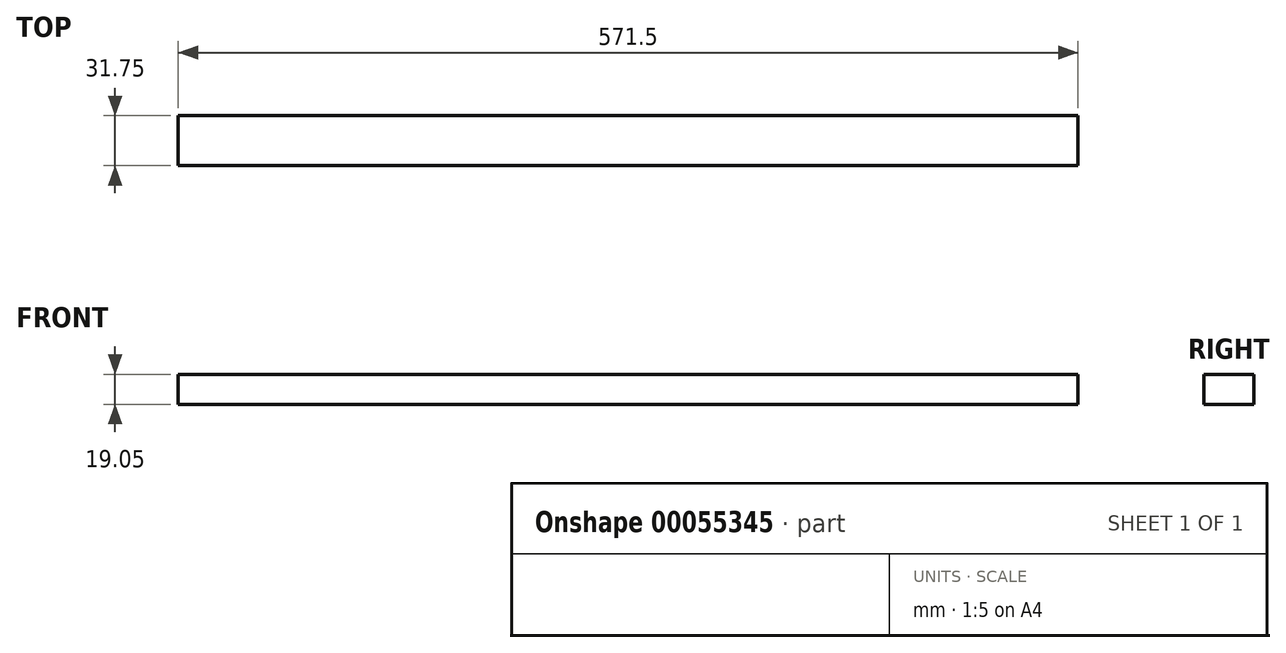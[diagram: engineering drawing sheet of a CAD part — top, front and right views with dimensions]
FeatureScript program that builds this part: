
annotation { "Feature Type Name" : "Feature", "Feature Type Description" : "" }
export const myFeature = defineFeature(function(context is Context, id is Id, definition is map)
    precondition{}
    {
        {
            var Q0;
            Q0=qCreatedBy(makeId("Front.planeOp"),FACE);
            var sketch = newSketch(context, id + "F0", { "sketchPlane" : qUnion([Q0])});
            skLineSegment(sketch, "E0.bottom", {"start": v(0, 0) * mm, "end": v(571.5, 0) * mm});
            skLineSegment(sketch, "E0.top", {"start": v(0, 19.05) * mm, "end": v(571.5, 19.05) * mm});
            skLineSegment(sketch, "E0.left", {"start": v(0, 0) * mm, "end": v(0, 19.05) * mm});
            skLineSegment(sketch, "E0.right", {"start": v(571.5, 0) * mm, "end": v(571.5, 19.05) * mm});
            skSolve(sketch);
        }
        {
            var Q0;
            Q0=makeQuery(id+"F0.imprint","IMPRINT",FACE,{"disambiguationData":[TD([[makeQuery(id+"F0.imprint","IMPRINT",EDGE,{"derivedFrom":sQuery(id+"F0.wireOp",EDGE,"E0.bottom")}),1.0]])]});
            extrude(context, id + "F1", {"entities" : qUnion([Q0]), "oppositeDirection" : true, "depth" : 31.75 * mm});
        }
        {
            var Q0;
            Q0=makeQuery(id+"F1.opExtrude","SWEPT_BODY",BODY,{"disambiguationData":[OSD([sQuery(id+"F0.wireOp",EDGE,"E0.bottom"),sQuery(id+"F0.wireOp",EDGE,"E0.top"),sQuery(id+"F0.wireOp",EDGE,"E0.left"),sQuery(id+"F0.wireOp",EDGE,"E0.right")])]});
            transform(context, id + "F2", {"entities" : qUnion([Q0]), "transformType" : TransformType.TRANSLATION_3D, "dx" : 0 * mm, "dy" : 0 * mm, "dz" : 0 * mm, "makeCopy" : true});
        }
        {
            var Q0;
            Q0=makeQuery(id+"F2.opPattern","COPY",BODY,{"derivedFrom":makeQuery(id+"F1.opExtrude","SWEPT_BODY",BODY,{"disambiguationData":[OSD([sQuery(id+"F0.wireOp",EDGE,"E0.bottom"),sQuery(id+"F0.wireOp",EDGE,"E0.top"),sQuery(id+"F0.wireOp",EDGE,"E0.left"),sQuery(id+"F0.wireOp",EDGE,"E0.right")])]}),"instanceName":"1"});
            deleteBodies(context, id + "F3", {"entities" : qUnion([Q0])});
        }
    });
